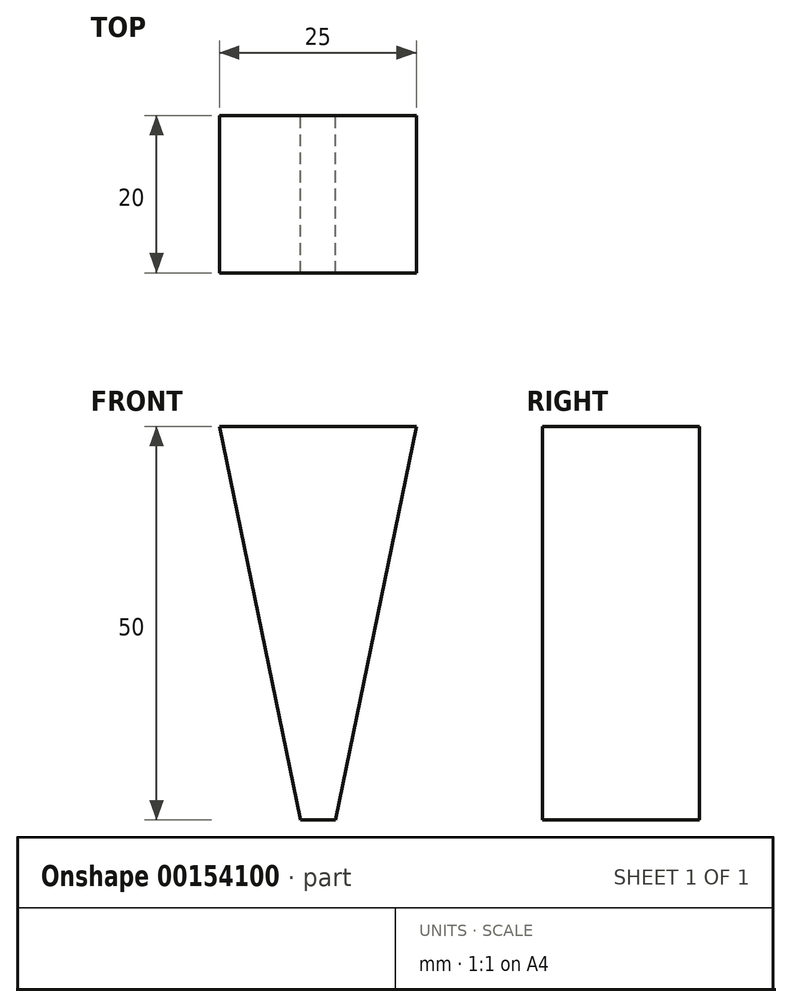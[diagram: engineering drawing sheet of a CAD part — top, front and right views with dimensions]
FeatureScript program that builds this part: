
annotation { "Feature Type Name" : "Feature", "Feature Type Description" : "" }
export const myFeature = defineFeature(function(context is Context, id is Id, definition is map)
    precondition{}
    {
        {
            var Q0;
            Q0=qCreatedBy(makeId("Front.planeOp"),FACE);
            var sketch = newSketch(context, id + "F0", { "sketchPlane" : qUnion([Q0])});
            skLineSegment(sketch, "E0", {"start": v(-12.5, 36.3) * mm, "end": v(12.5, 36.3) * mm});
            skLineSegment(sketch, "E1", {"start": v(-2.24, -13.7) * mm, "end": v(2.24, -13.7) * mm});
            skPoint(sketch, "E2", {"position": v(0, 36.3) * mm});
            skPoint(sketch, "E3", {"position": v(0, -13.7) * mm});
            skLineSegment(sketch, "E4", {"start": v(-12.5, 36.3) * mm, "end": v(-2.24, -13.7) * mm});
            skLineSegment(sketch, "E5", {"start": v(12.5, 36.3) * mm, "end": v(2.24, -13.7) * mm});
            skSolve(sketch);
        }
        {
            var Q0;
            Q0=makeQuery(id+"F0.imprint","IMPRINT",FACE,{"disambiguationData":[TD([[makeQuery(id+"F0.imprint","IMPRINT",EDGE,{"derivedFrom":sQuery(id+"F0.wireOp",EDGE,"E0")}),-1.0]])]});
            extrude(context, id + "F1", {"entities" : qUnion([Q0]), "depth" : 20 * mm});
        }
    });
